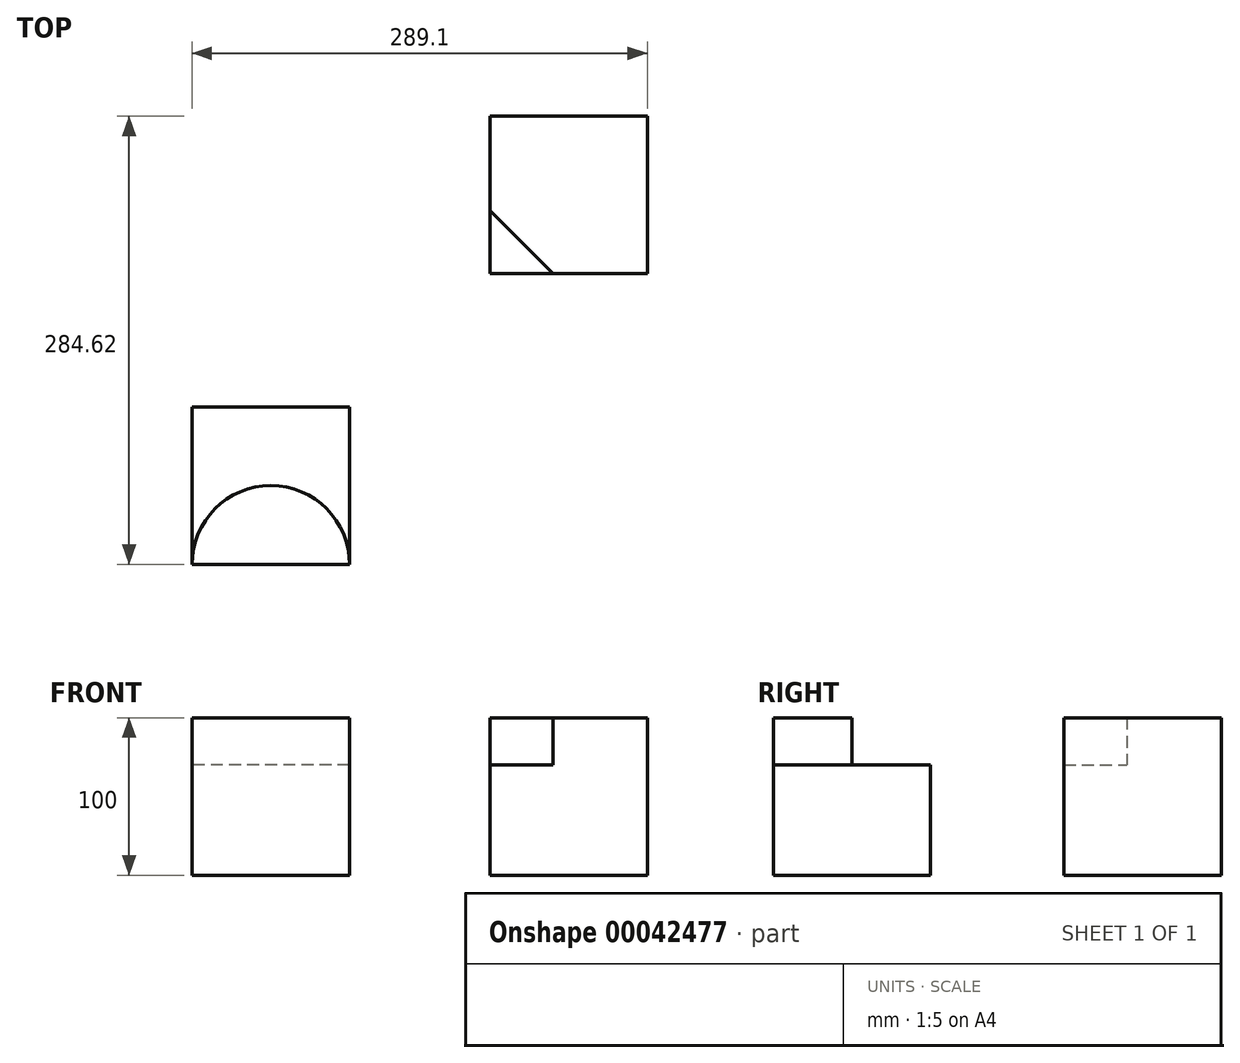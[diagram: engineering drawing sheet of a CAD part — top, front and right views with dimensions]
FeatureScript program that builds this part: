
annotation { "Feature Type Name" : "Feature", "Feature Type Description" : "" }
export const myFeature = defineFeature(function(context is Context, id is Id, definition is map)
    precondition{}
    {
        {
            var Q0;
            Q0=qCreatedBy(makeId("Top.planeOp"),FACE);
            var sketch = newSketch(context, id + "F0", { "sketchPlane" : qUnion([Q0])});
            skLineSegment(sketch, "E0.bottom", {"start": v(0, 0) * mm, "end": v(-100, 0) * mm});
            skLineSegment(sketch, "E0.top", {"start": v(0, 100) * mm, "end": v(-100, 100) * mm});
            skLineSegment(sketch, "E0.left", {"start": v(0, 0) * mm, "end": v(0, 100) * mm});
            skLineSegment(sketch, "E0.right", {"start": v(-100, 0) * mm, "end": v(-100, 100) * mm});
            skLineSegment(sketch, "E1", {"start": v(-100, 100) * mm, "end": v(-100, 40) * mm});
            skLineSegment(sketch, "E2", {"start": v(0, 0) * mm, "end": v(-60, 0) * mm});
            skLineSegment(sketch, "E3", {"start": v(-60, 0) * mm, "end": v(-100, 40) * mm});
            skSolve(sketch);
        }
        {
            var Q0;
            Q0=makeQuery(id+"F0.imprint","IMPRINT",FACE,{"disambiguationData":[TD([[makeQuery(id+"F0.imprint","IMPRINT",EDGE,{"derivedFrom":sQuery(id+"F0.wireOp",EDGE,"E0.top")}),1.0]])]});
            extrude(context, id + "F1", {"entities" : qUnion([Q0]), "depth" : 100 * mm});
        }
        {
            var Q0;
            Q0=makeQuery(id+"F0.imprint","IMPRINT",FACE,{"disambiguationData":[TD([[makeQuery(id+"F0.imprint","IMPRINT",EDGE,{"derivedFrom":sQuery(id+"F0.wireOp",EDGE,"E0.bottom")}),-1.0]])]});
            var Q1;
            Q1=makeQuery(id+"F0.imprint","IMPRINT",FACE,{"disambiguationData":[TD([[makeQuery(id+"F0.imprint","IMPRINT",EDGE,{"derivedFrom":sQuery(id+"F0.wireOp",EDGE,"E0.top")}),1.0]])]});
            extrude(context, id + "F2", {"entities" : qUnion([Q0, Q1]), "operationType" : NewBodyOperationType.ADD, "depth" : 70 * mm});
        }
        {
            var Q0;
            Q0=qCreatedBy(makeId("Top.planeOp"),FACE);
            var sketch = newSketch(context, id + "F3", { "sketchPlane" : qUnion([Q0])});
            skLineSegment(sketch, "E4.bottom", {"start": v(-189.1, -84.62) * mm, "end": v(-289.1, -84.62) * mm});
            skLineSegment(sketch, "E4.top", {"start": v(-189.1, -184.62) * mm, "end": v(-289.1, -184.62) * mm});
            skLineSegment(sketch, "E4.left", {"start": v(-189.1, -84.62) * mm, "end": v(-189.1, -184.62) * mm});
            skLineSegment(sketch, "E4.right", {"start": v(-289.1, -84.62) * mm, "end": v(-289.1, -184.62) * mm});
            skLineSegment(sketch, "E5.top", {"start": v(-189.1, -114.62) * mm, "end": v(-289.1, -114.62) * mm});
            skLineSegment(sketch, "E5.left", {"start": v(-189.1, -84.62) * mm, "end": v(-189.1, -114.62) * mm});
            skLineSegment(sketch, "E5.right", {"start": v(-289.1, -84.62) * mm, "end": v(-289.1, -114.62) * mm});
            skArc(sketch, "E6", {"start": v(-189.1, -184.62) * mm, "mid": v(-239.1, -134.62) * mm, "end": v(-289.1, -184.62) * mm});
            skSolve(sketch);
        }
        {
            var Q0;
            Q0=makeQuery(id+"F3.imprint","IMPRINT",FACE,{"disambiguationData":[TD([[makeQuery(id+"F3.imprint","IMPRINT",EDGE,{"derivedFrom":sQuery(id+"F3.wireOp",EDGE,"E4.bottom")}),1.0]])]});
            extrude(context, id + "F4", {"entities" : qUnion([Q0]), "depth" : 40 * mm});
        }
        {
            var Q0;
            Q0=makeQuery(id+"F3.imprint","IMPRINT",FACE,{"disambiguationData":[TD([[makeQuery(id+"F3.imprint","IMPRINT",EDGE,{"derivedFrom":sQuery(id+"F3.wireOp",EDGE,"E4.left")}),-1.0]])]});
            extrude(context, id + "F5", {"entities" : qUnion([Q0]), "operationType" : NewBodyOperationType.ADD, "depth" : 70 * mm});
        }
        {
            var Q0;
            Q0=makeQuery(id+"F3.imprint","IMPRINT",FACE,{"disambiguationData":[TD([[makeQuery(id+"F3.imprint","IMPRINT",EDGE,{"derivedFrom":sQuery(id+"F3.wireOp",EDGE,"E4.top")}),-1.0]])]});
            extrude(context, id + "F6", {"entities" : qUnion([Q0]), "operationType" : NewBodyOperationType.ADD, "depth" : 100 * mm});
        }
    });
